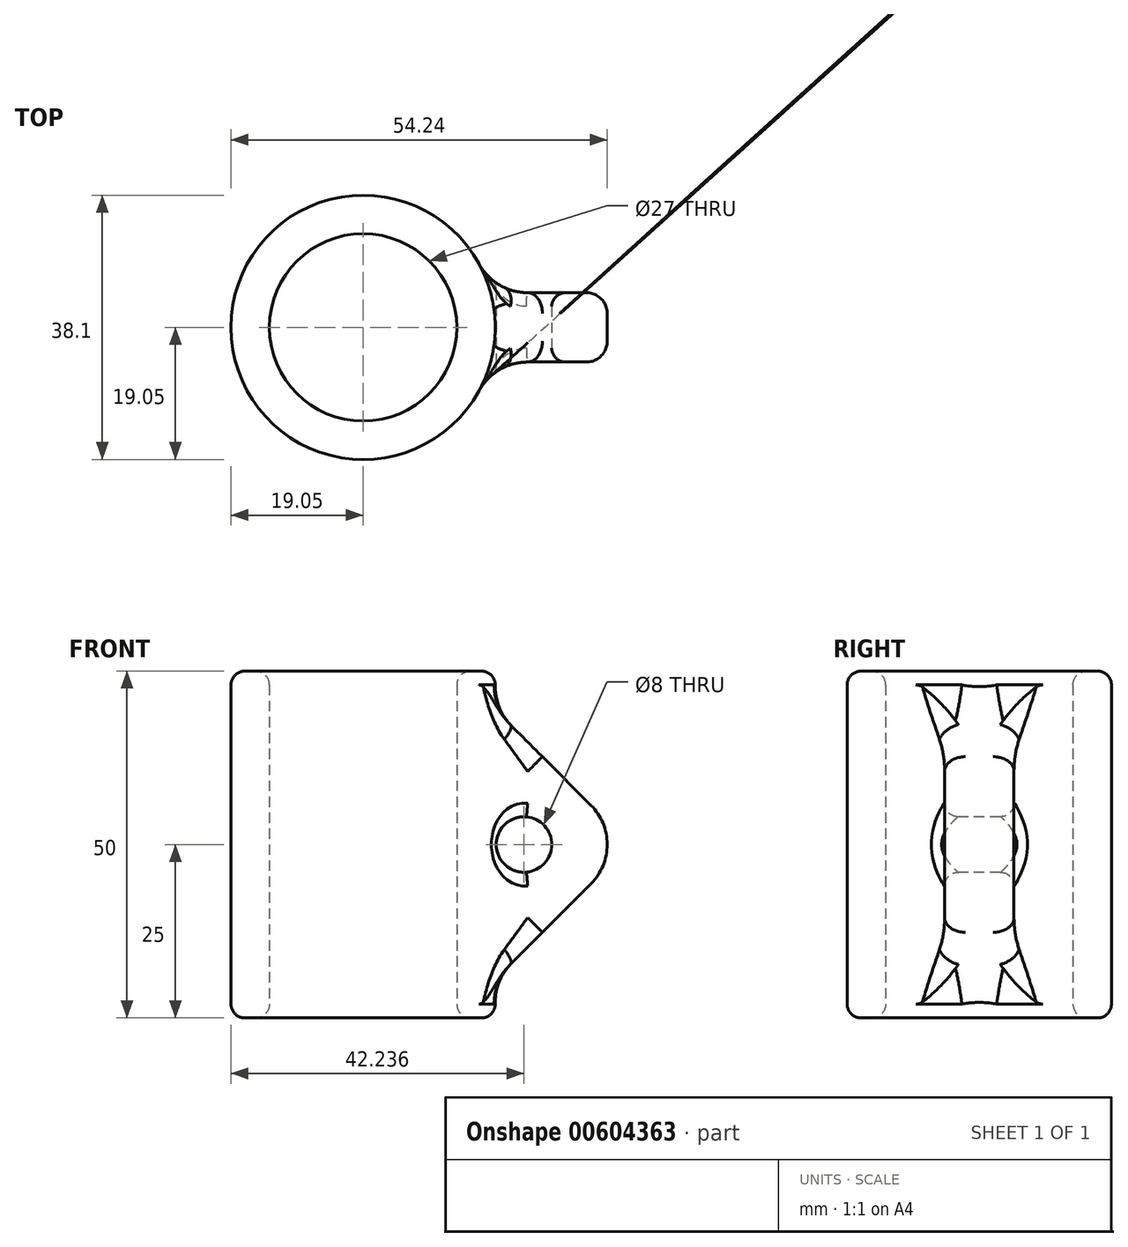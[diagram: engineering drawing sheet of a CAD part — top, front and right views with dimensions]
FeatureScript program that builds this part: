
annotation { "Feature Type Name" : "Feature", "Feature Type Description" : "" }
export const myFeature = defineFeature(function(context is Context, id is Id, definition is map)
    precondition{}
    {
        {
            var Q0;
            Q0=qCreatedBy(makeId("Top.planeOp"),FACE);
            var sketch = newSketch(context, id + "F0", { "sketchPlane" : qUnion([Q0])});
            skCircle(sketch, "E0", {"center": v(0, 0) * mm, "radius": 19.05 * mm});
            skCircle(sketch, "E1", {"center": v(0, 0) * mm, "radius": 13.5 * mm});
            skSolve(sketch);
        }
        {
            var Q0;
            Q0 = qSketchRegion(id + "F0", true);
            extrude(context, id + "F1", {"entities" : qUnion([Q0]), "endBound" : BoundingType.SYMMETRIC, "depth" : 50 * mm, "offsetDistance" : 25 * mm});
        }
        {
            var Q0;
            Q0=qCreatedBy(makeId("Front.planeOp"),FACE);
            var sketch = newSketch(context, id + "F2", { "sketchPlane" : qUnion([Q0])});
            skLineSegment(sketch, "E2", {"start": v(38.5, 0) * mm, "end": v(13.5, 0) * mm});
            skLineSegment(sketch, "E3", {"start": v(13.5, 0) * mm, "end": v(13.5, 25) * mm});
            skLineSegment(sketch, "E4", {"start": v(13.5, 25) * mm, "end": v(38.5, 0) * mm});
            skLineSegment(sketch, "E5", {"start": v(13.5, 0) * mm, "end": v(13.5, -25) * mm});
            skLineSegment(sketch, "E6", {"start": v(13.5, -25) * mm, "end": v(38.5, 0) * mm});
            skSolve(sketch);
        }
        {
            var Q0;
            Q0 = qSketchRegion(id + "F2", true);
            extrude(context, id + "F3", {"entities" : qUnion([Q0]), "operationType" : NewBodyOperationType.ADD, "endBound" : BoundingType.SYMMETRIC, "depth" : 10 * mm, "offsetDistance" : 25 * mm});
        }
        {
            var Q0;
            Q0=makeQuery(id+"F1.opExtrude","CAP_EDGE",EDGE,{"disambiguationData":[OSD([sQuery(id+"F0.wireOp",EDGE,"E0")])],"isStart":true});
            var Q1;
            Q1=makeQuery(id+"F1.opExtrude","CAP_EDGE",EDGE,{"disambiguationData":[OSD([sQuery(id+"F0.wireOp",EDGE,"E0")])],"isStart":false});
            var Q2;
            Q2=makeQuery(id+"F1.opExtrude","CAP_EDGE",EDGE,{"disambiguationData":[OSD([sQuery(id+"F0.wireOp",EDGE,"E1")])],"isStart":false});
            var Q3;
            Q3=makeQuery(id+"F1.opExtrude","CAP_EDGE",EDGE,{"disambiguationData":[OSD([sQuery(id+"F0.wireOp",EDGE,"E1")])],"isStart":true});
            fillet(context, id + "F4", {"entities" : qUnion([Q0, Q1, Q2, Q3]), "radius" : 2 * mm, "tangentPropagation" : true, "allowEdgeOverflow" : false});
        }
        {
            var Q0;
            Q0=makeQuery(id+"F3.boolean.opBoolean","INTERSECT",EDGE,{"derivedFrom":[makeQuery(id+"F1.opExtrude","SWEPT_FACE",FACE,{"disambiguationData":[OSD([sQuery(id+"F0.wireOp",EDGE,"E0")])]}),makeQuery(id+"F3.opExtrude","CAP_FACE",FACE,{"disambiguationData":[OSD([sQuery(id+"F2.wireOp",EDGE,"E3"),sQuery(id+"F2.wireOp",EDGE,"E4"),sQuery(id+"F2.wireOp",EDGE,"E5"),sQuery(id+"F2.wireOp",EDGE,"E6")])],"isStart":true})]});
            var Q1;
            Q1=makeQuery(id+"F3.boolean.opBoolean","INTERSECT",EDGE,{"derivedFrom":[makeQuery(id+"F1.opExtrude","SWEPT_FACE",FACE,{"disambiguationData":[OSD([sQuery(id+"F0.wireOp",EDGE,"E0")])]}),makeQuery(id+"F3.opExtrude","SWEPT_FACE",FACE,{"disambiguationData":[OSD([sQuery(id+"F2.wireOp",EDGE,"E6")])]})]});
            var Q2;
            Q2=makeQuery(id+"F3.boolean.opBoolean","INTERSECT",EDGE,{"derivedFrom":[makeQuery(id+"F1.opExtrude","SWEPT_FACE",FACE,{"disambiguationData":[OSD([sQuery(id+"F0.wireOp",EDGE,"E0")])]}),makeQuery(id+"F3.opExtrude","CAP_FACE",FACE,{"disambiguationData":[OSD([sQuery(id+"F2.wireOp",EDGE,"E3"),sQuery(id+"F2.wireOp",EDGE,"E4"),sQuery(id+"F2.wireOp",EDGE,"E5"),sQuery(id+"F2.wireOp",EDGE,"E6")])],"isStart":false})]});
            var Q3;
            Q3=makeQuery(id+"F3.boolean.opBoolean","INTERSECT",EDGE,{"derivedFrom":[makeQuery(id+"F1.opExtrude","SWEPT_FACE",FACE,{"disambiguationData":[OSD([sQuery(id+"F0.wireOp",EDGE,"E0")])]}),makeQuery(id+"F3.opExtrude","SWEPT_FACE",FACE,{"disambiguationData":[OSD([sQuery(id+"F2.wireOp",EDGE,"E4")])]})]});
            var Q4;
            Q4=makeQuery(id+"F3.opExtrude","SWEPT_EDGE",EDGE,{"disambiguationData":[OSD([sQuery(id+"F2.wireOp",EDGE,"E2"),sQuery(id+"F2.wireOp",EDGE,"E4"),sQuery(id+"F2.wireOp",EDGE,"E6")])]});
            fillet(context, id + "F5", {"entities" : qUnion([Q0, Q1, Q2, Q3, Q4]), "radius" : 8 * mm, "tangentPropagation" : true, "allowEdgeOverflow" : false});
        }
        {
            var Q0;
            {var subQ0=sQuery(id+"F2.wireOp",EDGE,"E4");Q0=makeQuery(id+"F5.opFillet","BLEND_EDGE",EDGE,{"blendedFrom":[makeQuery(id+"F3.boolean.opBoolean","INTERSECT",EDGE,{"derivedFrom":[makeQuery(id+"F1.opExtrude","SWEPT_FACE",FACE,{"disambiguationData":[OSD([sQuery(id+"F0.wireOp",EDGE,"E0")])]}),makeQuery(id+"F3.opExtrude","CAP_FACE",FACE,{"disambiguationData":[OSD([sQuery(id+"F2.wireOp",EDGE,"E3"),subQ0,sQuery(id+"F2.wireOp",EDGE,"E5"),sQuery(id+"F2.wireOp",EDGE,"E6")])],"isStart":false})]}),makeQuery(id+"F3.opExtrude","SWEPT_FACE",FACE,{"disambiguationData":[OSD([subQ0])]})],"blendedInto":[makeQuery(id+"F3.opExtrude","SWEPT_FACE",FACE,{"disambiguationData":[OSD([subQ0])]})]});}
            var Q1;
            Q1=makeQuery(id+"F3.opExtrude","CAP_EDGE",EDGE,{"disambiguationData":[OSD([sQuery(id+"F2.wireOp",EDGE,"E6")])],"isStart":true});
            fillet(context, id + "F6", {"entities" : qUnion([Q0, Q1]), "radius" : 3 * mm, "tangentPropagation" : true, "allowEdgeOverflow" : false});
        }
        {
            var Q0;
            Q0=makeQuery(id+"F3.opExtrude","CAP_FACE",FACE,{"disambiguationData":[OSD([sQuery(id+"F2.wireOp",EDGE,"E3"),sQuery(id+"F2.wireOp",EDGE,"E4"),sQuery(id+"F2.wireOp",EDGE,"E5"),sQuery(id+"F2.wireOp",EDGE,"E6")])],"isStart":false});
            var sketch = newSketch(context, id + "F7", { "sketchPlane" : qUnion([Q0])});
            skCircle(sketch, "E7", {"center": v(23.19, 0) * mm, "radius": 4 * mm});
            skSolve(sketch);
        }
        {
            var Q0;
            {var subQ0=sQuery(id+"F7.wireOp",EDGE,"E7");var subQ1=makeQuery(id+"F3.opExtrude","CAP_FACE",FACE,{"disambiguationData":[OSD([sQuery(id+"F2.wireOp",EDGE,"E3"),sQuery(id+"F2.wireOp",EDGE,"E4"),sQuery(id+"F2.wireOp",EDGE,"E5"),sQuery(id+"F2.wireOp",EDGE,"E6")])],"isStart":false});var subQ2=makeQuery(id+"F5.opFillet","BLEND_EDGE",EDGE,{"blendedFrom":[makeQuery(id+"F3.boolean.opBoolean","INTERSECT",EDGE,{"derivedFrom":[makeQuery(id+"F1.opExtrude","SWEPT_FACE",FACE,{"disambiguationData":[OSD([sQuery(id+"F0.wireOp",EDGE,"E0")])]}),subQ1]}),subQ1],"blendedInto":[subQ1]});var subQ3=makeQuery(id+"F7.imprint","INTERSECT",VERTEX,{"disambiguationData":[OD(0.0)],"derivedFrom":[subQ2,subQ0]});Q0=makeQuery(id+"F7.imprint","IMPRINT",FACE,{"disambiguationData":[TD([[makeQuery(id+"F7.imprint","IMPRINT",EDGE,{"disambiguationData":[TD([[subQ3,1.0]])],"derivedFrom":subQ0}),1.0]])]});}
            var Q1;
            {var subQ0=sQuery(id+"F7.wireOp",EDGE,"E7");var subQ1=makeQuery(id+"F3.opExtrude","CAP_FACE",FACE,{"disambiguationData":[OSD([sQuery(id+"F2.wireOp",EDGE,"E3"),sQuery(id+"F2.wireOp",EDGE,"E4"),sQuery(id+"F2.wireOp",EDGE,"E5"),sQuery(id+"F2.wireOp",EDGE,"E6")])],"isStart":false});var subQ2=makeQuery(id+"F5.opFillet","BLEND_EDGE",EDGE,{"blendedFrom":[makeQuery(id+"F3.boolean.opBoolean","INTERSECT",EDGE,{"derivedFrom":[makeQuery(id+"F1.opExtrude","SWEPT_FACE",FACE,{"disambiguationData":[OSD([sQuery(id+"F0.wireOp",EDGE,"E0")])]}),subQ1]}),subQ1],"blendedInto":[subQ1]});var subQ3=makeQuery(id+"F7.imprint","INTERSECT",VERTEX,{"disambiguationData":[OD(0.0)],"derivedFrom":[subQ2,subQ0]});Q1=makeQuery(id+"F7.imprint","IMPRINT",FACE,{"disambiguationData":[TD([[makeQuery(id+"F7.imprint","IMPRINT",EDGE,{"disambiguationData":[TD([[subQ3,-1.0]])],"derivedFrom":subQ0}),1.0]])]});}
            var Q2;
            Q2=sQuery(id+"F7.wireOp",EDGE,"E7");
            extrude(context, id + "F8", {"entities" : qUnion([Q0, Q1]), "operationType" : NewBodyOperationType.REMOVE, "surfaceEntities" : qUnion([Q2]), "oppositeDirection" : true, "depth" : 25 * mm, "offsetDistance" : 25 * mm, "hasSecondDirection" : true, "secondDirectionOppositeDirection" : false, "secondDirectionDepth" : 25 * mm});
        }
        {
            var Q0;
            Q0=makeQuery(id+"F8.boolean.opBoolean","INTERSECT",EDGE,{"derivedFrom":[makeQuery(id+"F3.opExtrude","CAP_FACE",FACE,{"disambiguationData":[OSD([sQuery(id+"F2.wireOp",EDGE,"E3"),sQuery(id+"F2.wireOp",EDGE,"E4"),sQuery(id+"F2.wireOp",EDGE,"E5"),sQuery(id+"F2.wireOp",EDGE,"E6")])],"isStart":false}),makeQuery(id+"F8.opExtrude","SWEPT_FACE",FACE,{"disambiguationData":[OSD([sQuery(id+"F7.wireOp",EDGE,"E7")])]})]});
            var Q1;
            {var subQ0=sQuery(id+"F2.wireOp",EDGE,"E6");var subQ1=sQuery(id+"F2.wireOp",EDGE,"E5");var subQ2=sQuery(id+"F2.wireOp",EDGE,"E4");var subQ3=sQuery(id+"F2.wireOp",EDGE,"E3");var subQ4=sQuery(id+"F0.wireOp",EDGE,"E0");Q1=makeQuery(id+"F8.boolean.opBoolean","INTERSECT",EDGE,{"derivedFrom":[makeQuery(id+"F5.opFillet","BLEND_FACE",FACE,{"disambiguationData":[OSD([subQ4,subQ3,subQ2,subQ1,subQ0]),TDD([makeQuery(id+"F3.boolean.opBoolean","INTERSECT",EDGE,{"derivedFrom":[makeQuery(id+"F1.opExtrude","SWEPT_FACE",FACE,{"disambiguationData":[OSD([subQ4])]}),makeQuery(id+"F3.opExtrude","CAP_FACE",FACE,{"disambiguationData":[OSD([subQ3,subQ2,subQ1,subQ0])],"isStart":false})]})])]}),makeQuery(id+"F8.opExtrude","SWEPT_FACE",FACE,{"disambiguationData":[OSD([sQuery(id+"F7.wireOp",EDGE,"E7")])]})]});}
            var Q2;
            Q2=makeQuery(id+"F8.boolean.opBoolean","INTERSECT",EDGE,{"derivedFrom":[makeQuery(id+"F3.opExtrude","CAP_FACE",FACE,{"disambiguationData":[OSD([sQuery(id+"F2.wireOp",EDGE,"E3"),sQuery(id+"F2.wireOp",EDGE,"E4"),sQuery(id+"F2.wireOp",EDGE,"E5"),sQuery(id+"F2.wireOp",EDGE,"E6")])],"isStart":true}),makeQuery(id+"F8.opExtrude","SWEPT_FACE",FACE,{"disambiguationData":[OSD([sQuery(id+"F7.wireOp",EDGE,"E7")])]})]});
            var Q3;
            {var subQ0=sQuery(id+"F2.wireOp",EDGE,"E6");var subQ1=sQuery(id+"F2.wireOp",EDGE,"E5");var subQ2=sQuery(id+"F2.wireOp",EDGE,"E4");var subQ3=sQuery(id+"F2.wireOp",EDGE,"E3");var subQ4=sQuery(id+"F0.wireOp",EDGE,"E0");Q3=makeQuery(id+"F8.boolean.opBoolean","INTERSECT",EDGE,{"derivedFrom":[makeQuery(id+"F5.opFillet","BLEND_FACE",FACE,{"disambiguationData":[OSD([subQ4,subQ3,subQ2,subQ1,subQ0]),TDD([makeQuery(id+"F3.boolean.opBoolean","INTERSECT",EDGE,{"derivedFrom":[makeQuery(id+"F1.opExtrude","SWEPT_FACE",FACE,{"disambiguationData":[OSD([subQ4])]}),makeQuery(id+"F3.opExtrude","CAP_FACE",FACE,{"disambiguationData":[OSD([subQ3,subQ2,subQ1,subQ0])],"isStart":true})]})])]}),makeQuery(id+"F8.opExtrude","SWEPT_FACE",FACE,{"disambiguationData":[OSD([sQuery(id+"F7.wireOp",EDGE,"E7")])]})]});}
            fillet(context, id + "F9", {"entities" : qUnion([Q0, Q1, Q2, Q3]), "radius" : 2 * mm, "tangentPropagation" : true, "allowEdgeOverflow" : false});
        }
    });
